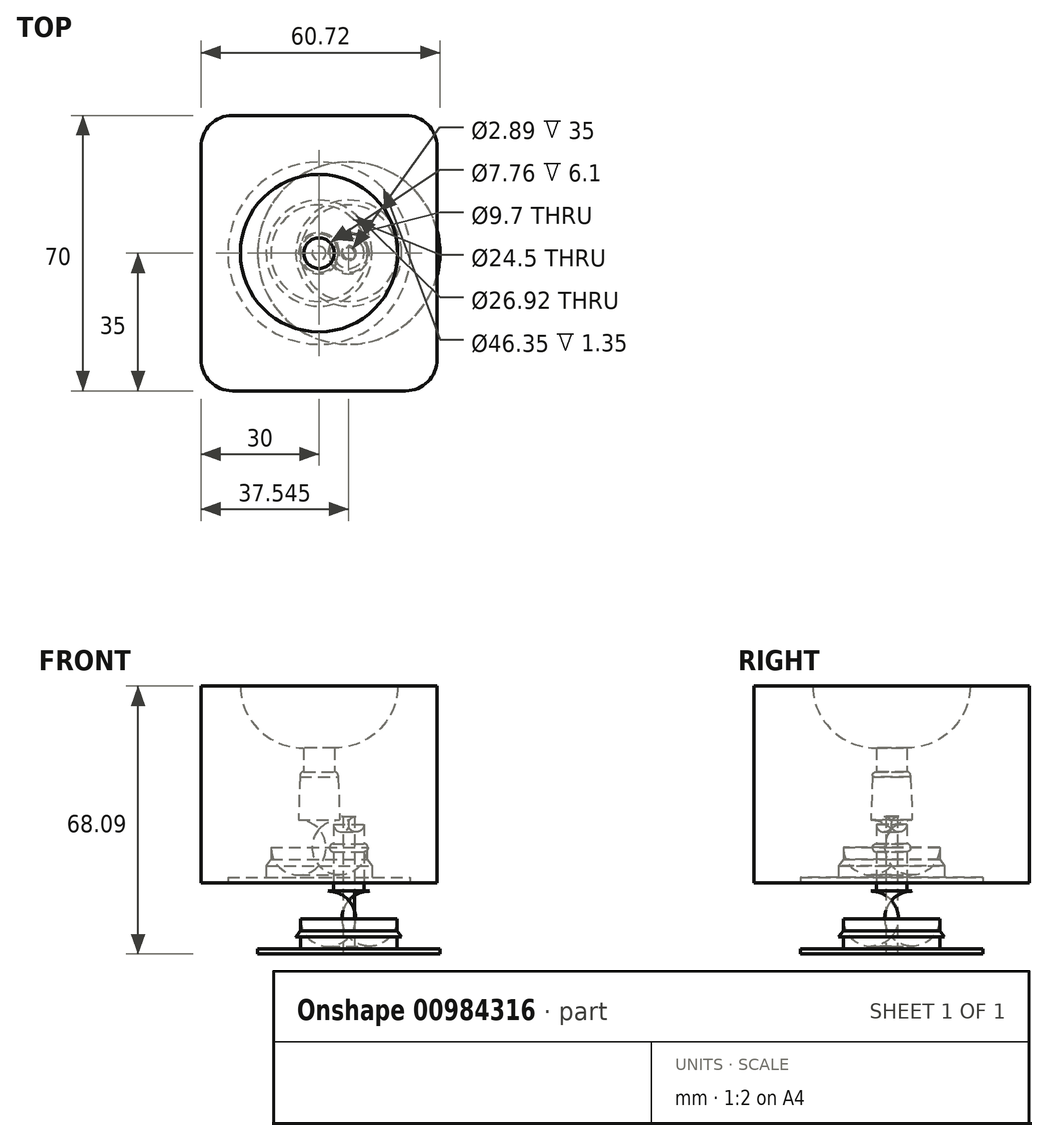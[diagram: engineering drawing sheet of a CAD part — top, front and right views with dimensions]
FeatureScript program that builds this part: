
annotation { "Feature Type Name" : "Feature", "Feature Type Description" : "" }
export const myFeature = defineFeature(function(context is Context, id is Id, definition is map)
    precondition{}
    {
        {
            var Q0;
            Q0=qCreatedBy(makeId("Front.planeOp"),FACE);
            var sketch = newSketch(context, id + "F0", { "sketchPlane" : qUnion([Q0])});
            skLineSegment(sketch, "E0", {"start": v(0, 0) * mm, "end": v(-23.18, 0) * mm});
            skLineSegment(sketch, "E1", {"start": v(-23.18, 0) * mm, "end": v(-23.18, 1.35) * mm});
            skLineSegment(sketch, "E2", {"start": v(-23.17, 1.35) * mm, "end": v(-12.25, 1.35) * mm});
            skLineSegment(sketch, "E3", {"start": v(-12.25, 1.35) * mm, "end": v(-12.25, 4.35) * mm});
            skLineSegment(sketch, "E4", {"start": v(-12.25, 4.35) * mm, "end": v(-13.46, 4.35) * mm, "construction": true});
            skLineSegment(sketch, "E5", {"start": v(-13.46, 4.35) * mm, "end": v(-12.25, 5.95) * mm});
            skLineSegment(sketch, "E6", {"start": v(-12.25, 5.95) * mm, "end": v(-12.25, 9) * mm});
            skLineSegment(sketch, "E7", {"start": v(-5.25, 16) * mm, "end": v(-3.88, 16) * mm});
            skLineSegment(sketch, "E8", {"start": v(-3.88, 16) * mm, "end": v(-3.88, 26) * mm});
            skLineSegment(sketch, "E9", {"start": v(-3.88, 26) * mm, "end": v(-3.95, 26) * mm});
            skLineSegment(sketch, "E10", {"start": v(-4.85, 26.9) * mm, "end": v(-4.85, 27.1) * mm});
            skLineSegment(sketch, "E11", {"start": v(-1.88, 35) * mm, "end": v(0, 35) * mm});
            skLineSegment(sketch, "E12", {"start": v(0, 35) * mm, "end": v(0, 0) * mm, "construction": true});
            skPoint(sketch, "E13.visualSharp", {"position": v(-12.25, 16) * mm});
            skArc(sketch, "E13.filletArc", {"start": v(-5.25, 16) * mm, "mid": v(-10.2, 13.95) * mm, "end": v(-12.25, 9) * mm});
            skLineSegment(sketch, "E14", {"start": v(0, 0) * mm, "end": v(0, 35) * mm});
            skPoint(sketch, "E15.visualSharp", {"position": v(-4.85, 28) * mm});
            skPoint(sketch, "E16.visualSharp", {"position": v(-4.85, 26) * mm});
            skArc(sketch, "E16.filletArc", {"start": v(-4.85, 26.9) * mm, "mid": v(-4.59, 26.26) * mm, "end": v(-3.95, 26) * mm});
            skPoint(sketch, "E17.visualSharp", {"position": v(-3.88, 35) * mm});
            skLineSegment(sketch, "E18", {"start": v(-12.25, 5.95) * mm, "end": v(-12.25, 4.35) * mm});
            skPoint(sketch, "E19.visualSharp", {"position": v(-13.98, 3.15) * mm});
            skPoint(sketch, "E20.visualSharp", {"position": v(-13.98, 6.23) * mm});
            skLineSegment(sketch, "E21", {"start": v(-3.88, 35) * mm, "end": v(-1.88, 35) * mm});
            skLineSegment(sketch, "E22", {"start": v(-4.85, 27.1) * mm, "end": v(-3.88, 27.1) * mm, "construction": true});
            skLineSegment(sketch, "E23.MirrorCS", {"start": v(-3.88, 28.2) * mm, "end": v(-3.95, 28.2) * mm});
            skArc(sketch, "E24.MirrorCS", {"start": v(-4.85, 27.3) * mm, "mid": v(-4.59, 27.94) * mm, "end": v(-3.95, 28.2) * mm});
            skLineSegment(sketch, "E25.MirrorCS", {"start": v(-4.85, 27.3) * mm, "end": v(-4.85, 27.1) * mm});
            skLineSegment(sketch, "E26", {"start": v(-3.88, 28.2) * mm, "end": v(-3.88, 35) * mm});
            skPoint(sketch, "E27.orphan", {"position": v(-4.85, 35) * mm});
            skLineSegment(sketch, "E28", {"start": v(-4.85, 26.9) * mm, "end": v(-5.25, 16) * mm});
            skLineSegment(sketch, "E29", {"start": v(-13.46, 4.35) * mm, "end": v(-13.46, 1.35) * mm});
            skSolve(sketch);
        }
        {
            var Q0;
            Q0 = qSketchRegion(id + "F0", true);
            var Q1;
            Q1=sQuery(id+"F0.wireOp",EDGE,"E14");
            revolve(context, id + "F1", {"surfaceOperationType" : NewSurfaceOperationType.NEW, "entities" : qUnion([Q0]), "axis" : qUnion([Q1]), "revolveType" : RevolveType.FULL});
        }
        {
            var Q0;
            Q0=qCreatedBy(makeId("Right.planeOp"),FACE);
            var sketch = newSketch(context, id + "F2", { "sketchPlane" : qUnion([Q0])});
            skLineSegment(sketch, "E30.bottom", {"start": v(-35, 0) * mm, "end": v(35, 0) * mm});
            skLineSegment(sketch, "E30.top", {"start": v(-35, 50) * mm, "end": v(35, 50) * mm});
            skLineSegment(sketch, "E30.left", {"start": v(-35, 0) * mm, "end": v(-35, 50) * mm});
            skLineSegment(sketch, "E30.right", {"start": v(35, 0) * mm, "end": v(35, 50) * mm});
            skPoint(sketch, "E31.visualSharp", {"position": v(-35, 50) * mm});
            skSolve(sketch);
        }
        {
            var Q0;
            Q0=makeQuery(id+"F2.imprint","IMPRINT",FACE,{"disambiguationData":[TD([[makeQuery(id+"F2.imprint","IMPRINT",EDGE,{"derivedFrom":sQuery(id+"F2.wireOp",EDGE,"E30.bottom")}),1.0]])]});
            extrude(context, id + "F3", {"entities" : qUnion([Q0]), "endBound" : BoundingType.SYMMETRIC, "depth" : 60 * mm, "offsetDistance" : 25 * mm});
        }
        {
            var Q0;
            Q0=makeQuery(id+"F3.opExtrude","CAP_EDGE",EDGE,{"disambiguationData":[OSD([sQuery(id+"F2.wireOp",EDGE,"E30.left")])],"isStart":false});
            var Q1;
            Q1=makeQuery(id+"F3.opExtrude","CAP_EDGE",EDGE,{"disambiguationData":[OSD([sQuery(id+"F2.wireOp",EDGE,"E30.right")])],"isStart":false});
            var Q2;
            Q2=makeQuery(id+"F3.opExtrude","CAP_EDGE",EDGE,{"disambiguationData":[OSD([sQuery(id+"F2.wireOp",EDGE,"E30.left")])],"isStart":true});
            var Q3;
            Q3=makeQuery(id+"F3.opExtrude","CAP_EDGE",EDGE,{"disambiguationData":[OSD([sQuery(id+"F2.wireOp",EDGE,"E30.right")])],"isStart":true});
            fillet(context, id + "F4", {"entities" : qUnion([Q0, Q1, Q2, Q3]), "radius" : 8 * mm, "tangentPropagation" : true, "allowEdgeOverflow" : false});
        }
        {
            var Q0;
            Q0=makeQuery(id+"F1.opRevolve","SWEPT_BODY",BODY,{"disambiguationData":[OSD([sQuery(id+"F0.wireOp",EDGE,"E0"),sQuery(id+"F0.wireOp",EDGE,"E1"),sQuery(id+"F0.wireOp",EDGE,"E2"),sQuery(id+"F0.wireOp",EDGE,"E3"),sQuery(id+"F0.wireOp",EDGE,"E4"),sQuery(id+"F0.wireOp",EDGE,"E5"),sQuery(id+"F0.wireOp",EDGE,"E6"),sQuery(id+"F0.wireOp",EDGE,"E7"),sQuery(id+"F0.wireOp",EDGE,"E8"),sQuery(id+"F0.wireOp",EDGE,"E9"),sQuery(id+"F0.wireOp",EDGE,"E10"),sQuery(id+"F0.wireOp",EDGE,"y0reNmYL-7l9J-sikF-ihzT-fKHTNHeywpji"),sQuery(id+"F0.wireOp",EDGE,"B3MXPibE-6143-AVkN-nT1L-lTXm46VGJ1av"),sQuery(id+"F0.wireOp",EDGE,"E11"),sQuery(id+"F0.wireOp",EDGE,"E13.filletArc"),sQuery(id+"F0.wireOp",EDGE,"E14"),sQuery(id+"F0.wireOp",EDGE,"E15.filletArc"),sQuery(id+"F0.wireOp",EDGE,"E16.filletArc"),sQuery(id+"F0.wireOp",EDGE,"E17.filletArc")])]});
            var Q1;
            Q1=makeQuery(id+"F3.opExtrude","SWEPT_BODY",BODY,{"disambiguationData":[OSD([sQuery(id+"F2.wireOp",EDGE,"E30.bottom"),sQuery(id+"F2.wireOp",EDGE,"E30.top"),sQuery(id+"F2.wireOp",EDGE,"E30.left"),sQuery(id+"F2.wireOp",EDGE,"E30.right")])]});
            booleanBodies(context, id + "F5", {"operationType" : BooleanOperationType.SUBTRACTION, "tools" : qUnion([Q0]), "targets" : qUnion([Q1]), "keepTools" : true});
        }
        {
            var Q0;
            Q0=makeQuery(id+"F3.opExtrude","SWEPT_FACE",FACE,{"disambiguationData":[OSD([sQuery(id+"F2.wireOp",EDGE,"E30.top")])]});
            var sketch = newSketch(context, id + "F6", { "sketchPlane" : qUnion([Q0])});
            skCircle(sketch, "E32", {"center": v(0, 0) * mm, "radius": 20 * mm});
            skSolve(sketch);
        }
        {
            var Q0;
            Q0=makeQuery(id+"F6.imprint","IMPRINT",FACE,{"disambiguationData":[TD([[makeQuery(id+"F6.imprint","IMPRINT",EDGE,{"derivedFrom":sQuery(id+"F6.wireOp",EDGE,"E32")}),1.0]])]});
            extrude(context, id + "F7", {"entities" : qUnion([Q0]), "operationType" : NewBodyOperationType.REMOVE, "oppositeDirection" : true, "depth" : 15.7 * mm, "offsetDistance" : 25 * mm});
        }
        {
            var Q0;
            Q0=makeQuery(id+"F7.boolean.opBoolean","COPY",EDGE,{"derivedFrom":makeQuery(id+"F7.opExtrude","CAP_EDGE",EDGE,{"disambiguationData":[OSD([sQuery(id+"F6.wireOp",EDGE,"E32")])],"isStart":false})});
            fillet(context, id + "F8", {"entities" : qUnion([Q0]), "radius" : 15.93 * mm, "tangentPropagation" : true, "allowEdgeOverflow" : false});
        }
        {
            var Q0;
            Q0=qCreatedBy(makeId("Front.planeOp"),FACE);
            var sketch = newSketch(context, id + "F9", { "sketchPlane" : qUnion([Q0])});
            skLineSegment(sketch, "E33", {"start": v(6.1, -18.09) * mm, "end": v(-15.63, -18.09) * mm});
            skLineSegment(sketch, "E34", {"start": v(-15.63, -18.09) * mm, "end": v(-15.63, -16.74) * mm});
            skLineSegment(sketch, "E35", {"start": v(-15.63, -16.74) * mm, "end": v(-4.7, -16.74) * mm});
            skLineSegment(sketch, "E36", {"start": v(-4.7, -16.74) * mm, "end": v(-4.7, -13.74) * mm});
            skLineSegment(sketch, "E37", {"start": v(-4.7, -13.74) * mm, "end": v(-5.92, -13.74) * mm});
            skLineSegment(sketch, "E38", {"start": v(-5.92, -13.74) * mm, "end": v(-4.7, -12.14) * mm});
            skLineSegment(sketch, "E39", {"start": v(-4.7, -12.14) * mm, "end": v(-4.7, -9.09) * mm});
            skLineSegment(sketch, "E40", {"start": v(2.3, -2.09) * mm, "end": v(3.66, -2.09) * mm});
            skLineSegment(sketch, "E41", {"start": v(3.66, -2.09) * mm, "end": v(3.66, 7.91) * mm});
            skLineSegment(sketch, "E42", {"start": v(3.66, 7.91) * mm, "end": v(3.6, 7.91) * mm});
            skLineSegment(sketch, "E43", {"start": v(2.7, 8.81) * mm, "end": v(2.7, 9.01) * mm});
            skLineSegment(sketch, "E44", {"start": v(3.6, 9.91) * mm, "end": v(3.66, 9.91) * mm});
            skLineSegment(sketch, "E45", {"start": v(3.66, 9.91) * mm, "end": v(3.66, 14.91) * mm});
            skLineSegment(sketch, "E46", {"start": v(5.66, 16.91) * mm, "end": v(6.1, 16.91) * mm});
            skPoint(sketch, "E47.visualSharp", {"position": v(-4.7, -2.09) * mm});
            skArc(sketch, "E47.filletArc", {"start": v(2.3, -2.09) * mm, "mid": v(-2.66, -4.14) * mm, "end": v(-4.7, -9.09) * mm});
            skLineSegment(sketch, "E48", {"start": v(7.54, -18.09) * mm, "end": v(7.54, 16.91) * mm, "construction": true});
            skPoint(sketch, "E49.visualSharp", {"position": v(2.7, 9.91) * mm});
            skArc(sketch, "E49.filletArc", {"start": v(3.6, 9.91) * mm, "mid": v(2.96, 9.65) * mm, "end": v(2.7, 9.01) * mm});
            skPoint(sketch, "E50.visualSharp", {"position": v(2.7, 7.91) * mm});
            skArc(sketch, "E50.filletArc", {"start": v(2.7, 8.81) * mm, "mid": v(2.96, 8.17) * mm, "end": v(3.6, 7.91) * mm});
            skPoint(sketch, "E51.visualSharp", {"position": v(3.66, 16.91) * mm});
            skArc(sketch, "E51.filletArc", {"start": v(5.66, 16.91) * mm, "mid": v(4.25, 16.33) * mm, "end": v(3.66, 14.91) * mm});
            skLineSegment(sketch, "E52", {"start": v(-4.7, -12.14) * mm, "end": v(-4.7, -13.74) * mm, "construction": true});
            skLineSegment(sketch, "E53", {"start": v(6.1, -18.09) * mm, "end": v(6.1, 16.91) * mm});
            skSolve(sketch);
        }
        {
            var Q0;
            Q0 = qSketchRegion(id + "F9", true);
            var Q1;
            Q1=sQuery(id+"F9.wireOp",EDGE,"E48");
            revolve(context, id + "F10", {"surfaceOperationType" : NewSurfaceOperationType.NEW, "entities" : qUnion([Q0]), "axis" : qUnion([Q1]), "revolveType" : RevolveType.FULL});
        }
    });
